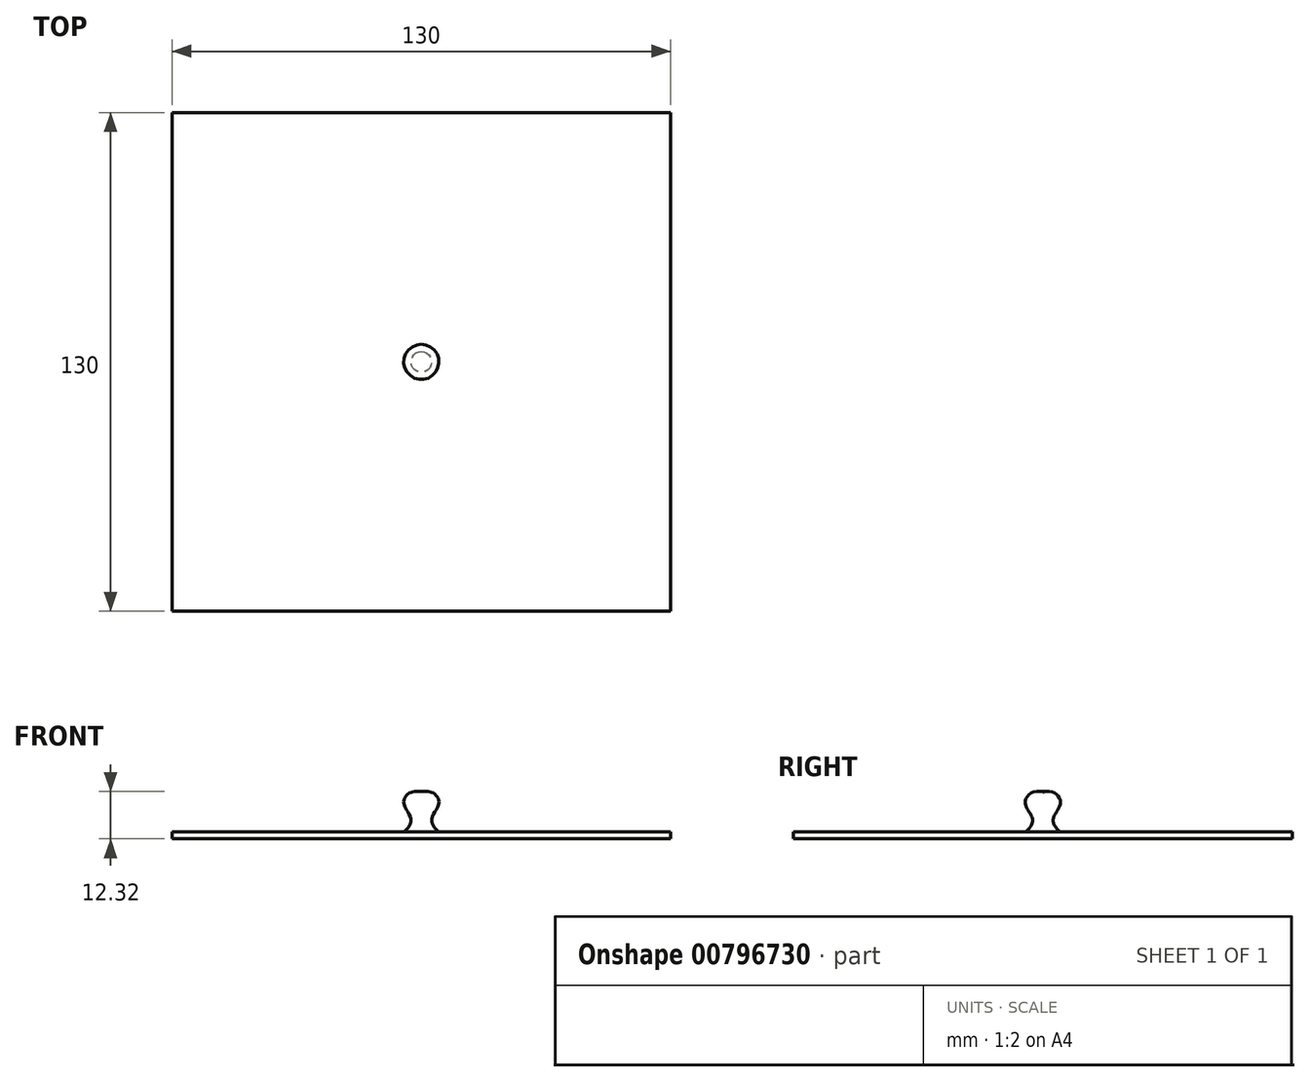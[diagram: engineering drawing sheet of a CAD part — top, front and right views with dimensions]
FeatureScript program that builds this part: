
annotation { "Feature Type Name" : "Feature", "Feature Type Description" : "" }
export const myFeature = defineFeature(function(context is Context, id is Id, definition is map)
    precondition{}
    {
        {
            var Q0;
            Q0=qCreatedBy(makeId("Top.planeOp"),FACE);
            var sketch = newSketch(context, id + "F0", { "sketchPlane" : qUnion([Q0])});
            skLineSegment(sketch, "E0.bottom", {"start": v(-65, 65) * mm, "end": v(65, 65) * mm});
            skLineSegment(sketch, "E0.top", {"start": v(-65, -65) * mm, "end": v(65, -65) * mm});
            skLineSegment(sketch, "E0.left", {"start": v(-65, 65) * mm, "end": v(-65, -65) * mm});
            skLineSegment(sketch, "E0.right", {"start": v(65, 65) * mm, "end": v(65, -65) * mm});
            skPoint(sketch, "E0.middle", {"position": v(0, 0) * mm});
            skSolve(sketch);
        }
        {
            var Q0;
            Q0=makeQuery(id+"F0.imprint","IMPRINT",FACE,{"disambiguationData":[TD([[makeQuery(id+"F0.imprint","IMPRINT",EDGE,{"derivedFrom":sQuery(id+"F0.wireOp",EDGE,"E0.bottom")}),-1.0]])]});
            extrude(context, id + "F1", {"entities" : qUnion([Q0]), "depth" : 1.8 * mm, "offsetDistance" : 25 * mm});
        }
        {
            var Q0;
            Q0=qCreatedBy(makeId("Right.planeOp"),FACE);
            var sketch = newSketch(context, id + "F2", { "sketchPlane" : qUnion([Q0])});
            skLineSegment(sketch, "E1", {"start": v(0, 11.8) * mm, "end": v(0, 1.8) * mm});
            skFitSpline(sketch, "E2", {"points": [v(4.51, 1.8) * mm, v(2.79, 5.5) * mm, v(4.58, 9.76) * mm, v(0, 11.8) * mm], "startDerivative": vector(-13.46, 11.22) * mm, "endDerivative": vector(-20.25, -12.34) * mm});
            skLineSegment(sketch, "E3", {"start": v(4.51, 1.8) * mm, "end": v(0, 1.8) * mm});
            skSolve(sketch);
        }
        {
            var Q0;
            Q0=makeQuery(id+"F2.imprint","IMPRINT",FACE,{"disambiguationData":[TD([[makeQuery(id+"F2.imprint","IMPRINT",EDGE,{"derivedFrom":sQuery(id+"F2.wireOp",EDGE,"E1")}),1.0]])]});
            var Q1;
            Q1=sQuery(id+"F2.wireOp",EDGE,"E1");
            revolve(context, id + "F3", {"operationType" : NewBodyOperationType.ADD, "surfaceOperationType" : NewSurfaceOperationType.NEW, "entities" : qUnion([Q0]), "axis" : qUnion([Q1]), "revolveType" : RevolveType.FULL});
        }
    });
